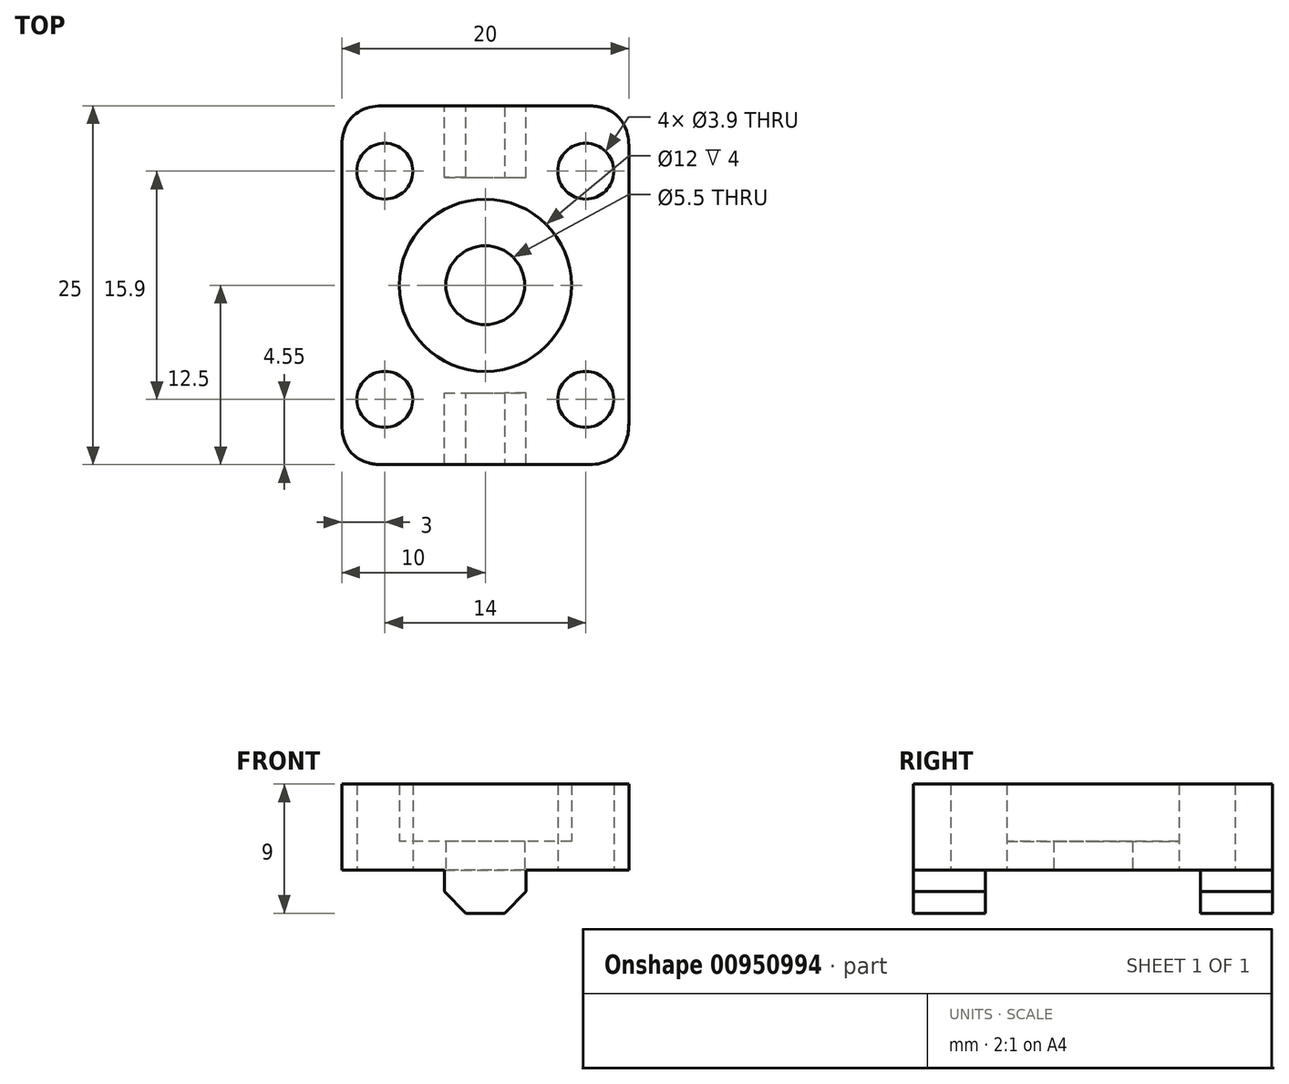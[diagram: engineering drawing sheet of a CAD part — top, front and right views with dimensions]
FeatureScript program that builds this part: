
annotation { "Feature Type Name" : "Feature", "Feature Type Description" : "" }
export const myFeature = defineFeature(function(context is Context, id is Id, definition is map)
    precondition{}
    {
        {
            var Q0;
            Q0=qCreatedBy(makeId("Top.planeOp"),FACE);
            var sketch = newSketch(context, id + "F0", { "sketchPlane" : qUnion([Q0])});
            skCircle(sketch, "E0", {"center": v(0, 0) * mm, "radius": 6 * mm});
            skCircle(sketch, "E1", {"center": v(0, 0) * mm, "radius": 2.75 * mm});
            skCircle(sketch, "E2", {"center": v(-7, 7.95) * mm, "radius": 1.95 * mm});
            skLineSegment(sketch, "E3.bottom", {"start": v(-10, 12.5) * mm, "end": v(10, 12.5) * mm});
            skLineSegment(sketch, "E3.top", {"start": v(-10, -12.5) * mm, "end": v(10, -12.5) * mm});
            skLineSegment(sketch, "E3.left", {"start": v(-10, 12.5) * mm, "end": v(-10, -12.5) * mm});
            skLineSegment(sketch, "E3.right", {"start": v(10, 12.5) * mm, "end": v(10, -12.5) * mm});
            skCircle(sketch, "E4.MirrorC", {"center": v(7, 7.95) * mm, "radius": 1.95 * mm});
            skCircle(sketch, "E5.MirrorC", {"center": v(7, -7.95) * mm, "radius": 1.95 * mm});
            skCircle(sketch, "E6.MirrorC", {"center": v(-7, -7.95) * mm, "radius": 1.95 * mm});
            skSolve(sketch);
        }
        {
            var Q0;
            Q0=makeQuery(id+"F0.imprint","IMPRINT",FACE,{"disambiguationData":[TD([[makeQuery(id+"F0.imprint","IMPRINT",EDGE,{"derivedFrom":sQuery(id+"F0.wireOp",EDGE,"E0")}),-1.0]])]});
            extrude(context, id + "F1", {"entities" : qUnion([Q0]), "depth" : 4 * mm, "offsetDistance" : 25 * mm});
        }
        {
            var Q0;
            Q0=makeQuery(id+"F1.opExtrude","CAP_FACE",FACE,{"disambiguationData":[OSD([sQuery(id+"F0.wireOp",EDGE,"E0"),sQuery(id+"F0.wireOp",EDGE,"E2"),sQuery(id+"F0.wireOp",EDGE,"E3.bottom"),sQuery(id+"F0.wireOp",EDGE,"E3.top"),sQuery(id+"F0.wireOp",EDGE,"E3.left"),sQuery(id+"F0.wireOp",EDGE,"E3.right"),sQuery(id+"F0.wireOp",EDGE,"E4.MirrorC"),sQuery(id+"F0.wireOp",EDGE,"E5.MirrorC"),sQuery(id+"F0.wireOp",EDGE,"E6.MirrorC")])],"isStart":false});
            var Q1;
            Q1=makeQuery(id+"F0.imprint","IMPRINT",FACE,{"disambiguationData":[TD([[makeQuery(id+"F0.imprint","IMPRINT",EDGE,{"derivedFrom":sQuery(id+"F0.wireOp",EDGE,"E0")}),1.0]])]});
            extrude(context, id + "F2", {"entities" : qUnion([Q0, Q1]), "operationType" : NewBodyOperationType.ADD, "depth" : 2 * mm, "offsetDistance" : 25 * mm});
        }
        {
            var Q0;
            {var subQ0=sQuery(id+"F0.wireOp",EDGE,"E3.right");var subQ1=sQuery(id+"F0.wireOp",EDGE,"E3.top");Q0=makeQuery(id+"F2.boolean.opBoolean","MERGE",EDGE,{"derivedFrom":[makeQuery(id+"F1.opExtrude","SWEPT_EDGE",EDGE,{"disambiguationData":[OSD([subQ1,subQ0])]}),makeQuery(id+"F2.opExtrude","SWEPT_EDGE",EDGE,{"disambiguationData":[OSD([subQ1,subQ0])]})]});}
            var Q1;
            {var subQ0=sQuery(id+"F0.wireOp",EDGE,"E3.right");var subQ1=sQuery(id+"F0.wireOp",EDGE,"E3.bottom");Q1=makeQuery(id+"F2.boolean.opBoolean","MERGE",EDGE,{"derivedFrom":[makeQuery(id+"F1.opExtrude","SWEPT_EDGE",EDGE,{"disambiguationData":[OSD([subQ1,subQ0])]}),makeQuery(id+"F2.opExtrude","SWEPT_EDGE",EDGE,{"disambiguationData":[OSD([subQ1,subQ0])]})]});}
            var Q2;
            {var subQ0=sQuery(id+"F0.wireOp",EDGE,"E3.left");var subQ1=sQuery(id+"F0.wireOp",EDGE,"E3.bottom");Q2=makeQuery(id+"F2.boolean.opBoolean","MERGE",EDGE,{"derivedFrom":[makeQuery(id+"F1.opExtrude","SWEPT_EDGE",EDGE,{"disambiguationData":[OSD([subQ1,subQ0])]}),makeQuery(id+"F2.opExtrude","SWEPT_EDGE",EDGE,{"disambiguationData":[OSD([subQ1,subQ0])]})]});}
            var Q3;
            {var subQ0=sQuery(id+"F0.wireOp",EDGE,"E3.left");var subQ1=sQuery(id+"F0.wireOp",EDGE,"E3.top");Q3=makeQuery(id+"F2.boolean.opBoolean","MERGE",EDGE,{"derivedFrom":[makeQuery(id+"F1.opExtrude","SWEPT_EDGE",EDGE,{"disambiguationData":[OSD([subQ1,subQ0])]}),makeQuery(id+"F2.opExtrude","SWEPT_EDGE",EDGE,{"disambiguationData":[OSD([subQ1,subQ0])]})]});}
            fillet(context, id + "F3", {"entities" : qUnion([Q0, Q1, Q2, Q3]), "tangentPropagation" : true, "crossSection" : FilletCrossSection.CURVATURE, "radius" : 3 * mm, "magnitude" : 0.5, "defaultsChanged" : true, "vertexSettings" : []});
        }
        {
            var Q0;
            Q0=makeQuery(id+"F0.imprint","IMPRINT",FACE,{"disambiguationData":[TD([[makeQuery(id+"F0.imprint","IMPRINT",EDGE,{"derivedFrom":sQuery(id+"F0.wireOp",EDGE,"E0")}),-1.0]])]});
            var sketch = newSketch(context, id + "F4", { "sketchPlane" : qUnion([Q0])});
            skLineSegment(sketch, "E7.0", {"start": v(-10, -12.5) * mm, "end": v(10, -12.5) * mm});
            skLineSegment(sketch, "E8.0", {"start": v(-10, 12.5) * mm, "end": v(10, 12.5) * mm});
            skLineSegment(sketch, "E9.bottom", {"start": v(-2.85, -12.5) * mm, "end": v(2.85, -12.5) * mm});
            skLineSegment(sketch, "E9.top", {"start": v(-2.85, 12.5) * mm, "end": v(2.85, 12.5) * mm});
            skLineSegment(sketch, "E9.left", {"start": v(-2.85, -12.5) * mm, "end": v(-2.85, 12.5) * mm});
            skLineSegment(sketch, "E9.right", {"start": v(2.85, -12.5) * mm, "end": v(2.85, 12.5) * mm});
            skLineSegment(sketch, "E10", {"start": v(-2.85, -7.5) * mm, "end": v(2.85, -7.5) * mm});
            skLineSegment(sketch, "E11.MirrorCS", {"start": v(-2.85, 7.5) * mm, "end": v(2.85, 7.5) * mm});
            skSolve(sketch);
        }
        {
            var Q0;
            {var subQ5=sQuery(id+"F4.wireOp",EDGE,"E10");Q0=makeQuery(id+"F4.imprint","IMPRINT",FACE,{"disambiguationData":[TD([[makeQuery(id+"F4.imprint","IMPRINT",EDGE,{"derivedFrom":subQ5}),-1.0]])]});}
            var Q1;
            {var subQ5=sQuery(id+"F4.wireOp",EDGE,"E11.MirrorCS");Q1=makeQuery(id+"F4.imprint","IMPRINT",FACE,{"disambiguationData":[TD([[makeQuery(id+"F4.imprint","IMPRINT",EDGE,{"derivedFrom":subQ5}),1.0]])]});}
            extrude(context, id + "F5", {"entities" : qUnion([Q0, Q1]), "operationType" : NewBodyOperationType.ADD, "oppositeDirection" : true, "depth" : 3 * mm, "offsetDistance" : 25 * mm});
        }
        {
            var Q0;
            {var subQ0=sQuery(id+"F4.wireOp",EDGE,"E9.right");Q0=makeQuery(id+"F5.opExtrude","CAP_EDGE",EDGE,{"disambiguationData":[OSD([subQ0]),TDD([makeQuery(id+"F4.imprint","IMPRINT",EDGE,{"disambiguationData":[TD([[makeQuery(id+"F4.imprint","INTERSECT",VERTEX,{"derivedFrom":[subQ0,sQuery(id+"F4.wireOp",EDGE,"E10")]}),1.0]])],"derivedFrom":subQ0})])],"isStart":false});}
            var Q1;
            {var subQ0=sQuery(id+"F4.wireOp",EDGE,"E9.left");Q1=makeQuery(id+"F5.opExtrude","CAP_EDGE",EDGE,{"disambiguationData":[OSD([subQ0]),TDD([makeQuery(id+"F4.imprint","IMPRINT",EDGE,{"disambiguationData":[TD([[makeQuery(id+"F4.imprint","INTERSECT",VERTEX,{"derivedFrom":[subQ0,sQuery(id+"F4.wireOp",EDGE,"E10")]}),1.0]])],"derivedFrom":subQ0})])],"isStart":false});}
            var Q2;
            {var subQ0=sQuery(id+"F4.wireOp",EDGE,"E9.right");Q2=makeQuery(id+"F5.opExtrude","CAP_EDGE",EDGE,{"disambiguationData":[OSD([subQ0]),TDD([makeQuery(id+"F4.imprint","IMPRINT",EDGE,{"disambiguationData":[TD([[makeQuery(id+"F4.imprint","INTERSECT",VERTEX,{"derivedFrom":[subQ0,sQuery(id+"F4.wireOp",EDGE,"E11.MirrorCS")]}),-1.0]])],"derivedFrom":subQ0})])],"isStart":false});}
            var Q3;
            {var subQ0=sQuery(id+"F4.wireOp",EDGE,"E9.left");Q3=makeQuery(id+"F5.opExtrude","CAP_EDGE",EDGE,{"disambiguationData":[OSD([subQ0]),TDD([makeQuery(id+"F4.imprint","IMPRINT",EDGE,{"disambiguationData":[TD([[makeQuery(id+"F4.imprint","INTERSECT",VERTEX,{"derivedFrom":[subQ0,sQuery(id+"F4.wireOp",EDGE,"E11.MirrorCS")]}),-1.0]])],"derivedFrom":subQ0})])],"isStart":false});}
            chamfer(context, id + "F6", {"entities" : qUnion([Q0, Q1, Q2, Q3]), "width" : 1.5 * mm, "tangentPropagation" : true});
        }
    });
